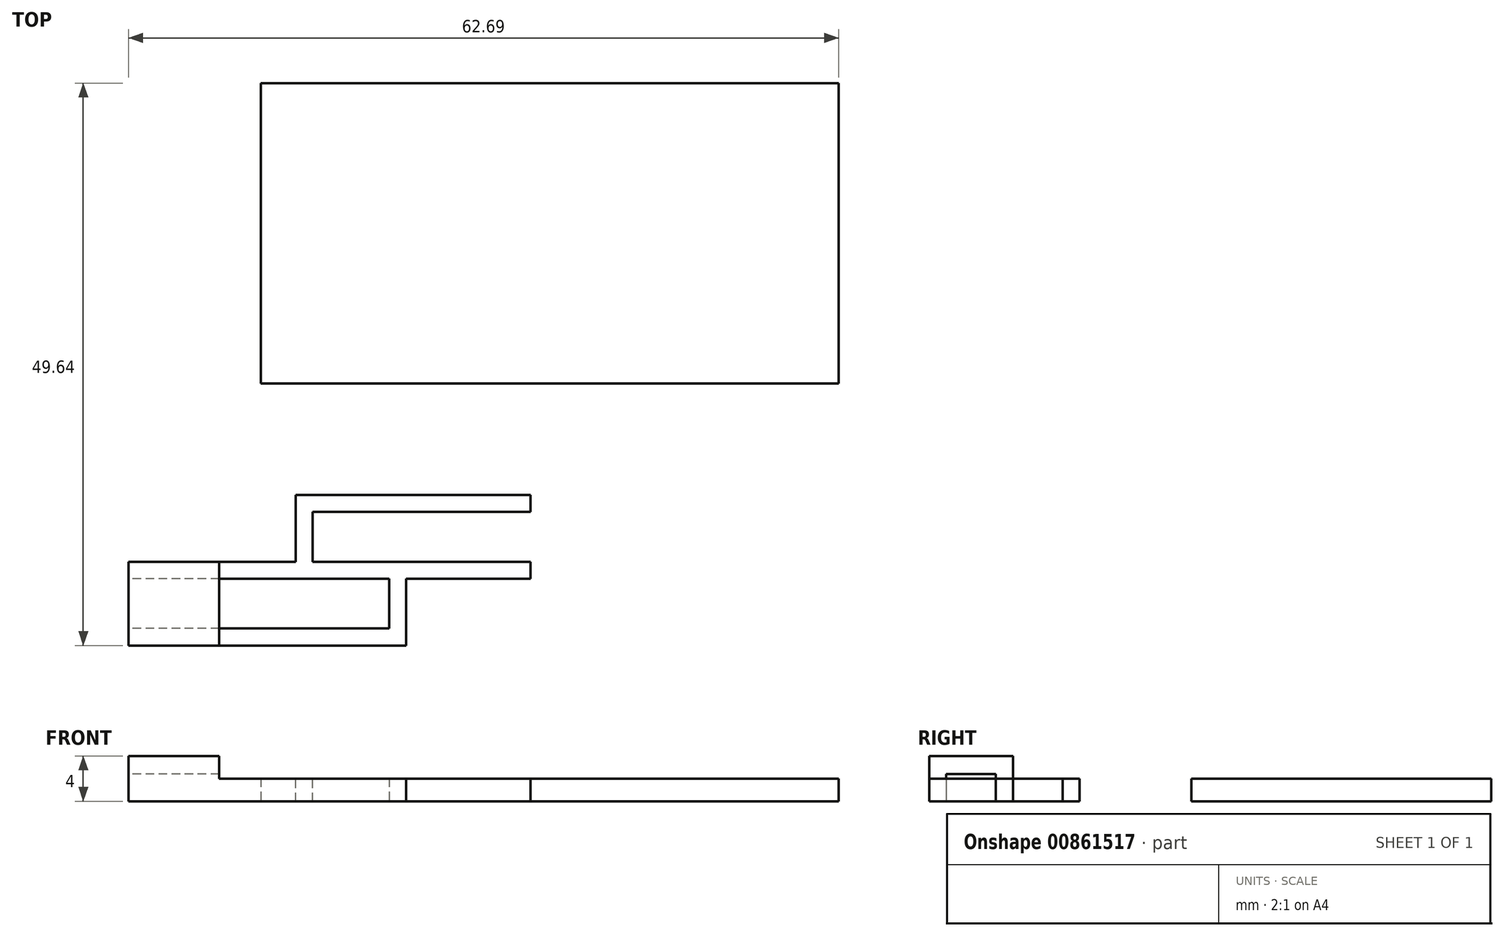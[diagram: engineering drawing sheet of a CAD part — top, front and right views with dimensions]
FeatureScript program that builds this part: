
annotation { "Feature Type Name" : "Feature", "Feature Type Description" : "" }
export const myFeature = defineFeature(function(context is Context, id is Id, definition is map)
    precondition{}
    {
        {
            var Q0;
            Q0=qCreatedBy(makeId("Top.planeOp"),FACE);
            var sketch = newSketch(context, id + "F0", { "sketchPlane" : qUnion([Q0])});
            skLineSegment(sketch, "E0.bottom", {"start": v(25.5, -13.25) * mm, "end": v(-25.5, -13.25) * mm});
            skLineSegment(sketch, "E0.top", {"start": v(25.5, 13.25) * mm, "end": v(-25.5, 13.25) * mm});
            skLineSegment(sketch, "E0.left", {"start": v(25.5, -13.25) * mm, "end": v(25.5, 13.25) * mm});
            skLineSegment(sketch, "E0.right", {"start": v(-25.5, -13.25) * mm, "end": v(-25.5, 13.25) * mm});
            skPoint(sketch, "E0.middle", {"position": v(0, 0) * mm});
            skSolve(sketch);
        }
        {
            var Q0;
            Q0 = qSketchRegion(id + "F0", true);
            extrude(context, id + "F1", {"entities" : qUnion([Q0]), "depth" : 2 * mm, "offsetDistance" : 25.4 * mm});
        }
        {
            var Q0;
            Q0=qCreatedBy(makeId("Top.planeOp"),FACE);
            var sketch = newSketch(context, id + "F2", { "sketchPlane" : qUnion([Q0])});
            skLineSegment(sketch, "E1.bottom", {"start": v(-37.2, -29) * mm, "end": v(-12.7, -29) * mm});
            skLineSegment(sketch, "E1.top", {"start": v(-37.2, -36.4) * mm, "end": v(-12.7, -36.4) * mm});
            skLineSegment(sketch, "E1.left", {"start": v(-37.2, -29) * mm, "end": v(-37.2, -36.4) * mm});
            skLineSegment(sketch, "E1.right", {"start": v(-12.7, -29) * mm, "end": v(-12.7, -36.4) * mm});
            skSolve(sketch);
        }
        {
            var Q0;
            Q0=makeQuery(id+"F2.imprint","IMPRINT",FACE,{"disambiguationData":[TD([[makeQuery(id+"F2.imprint","IMPRINT",EDGE,{"derivedFrom":sQuery(id+"F2.wireOp",EDGE,"E1.bottom")}),-1.0]])]});
            extrude(context, id + "F3", {"entities" : qUnion([Q0]), "depth" : 4 * mm, "offsetDistance" : 25 * mm});
        }
        {
            var Q0;
            Q0=makeQuery(id+"F3.opExtrude","SWEPT_FACE",FACE,{"disambiguationData":[OSD([sQuery(id+"F2.wireOp",EDGE,"E1.left")])]});
            var sketch = newSketch(context, id + "F4", { "sketchPlane" : qUnion([Q0])});
            skLineSegment(sketch, "E2", {"start": v(32.7, 4) * mm, "end": v(32.7, 0) * mm, "construction": true});
            skLineSegment(sketch, "E3.bottom", {"start": v(30.5, 2.4) * mm, "end": v(34.9, 2.4) * mm});
            skLineSegment(sketch, "E3.top", {"start": v(30.5, 0) * mm, "end": v(34.9, 0) * mm});
            skLineSegment(sketch, "E3.left", {"start": v(30.5, 2.4) * mm, "end": v(30.5, 0) * mm});
            skLineSegment(sketch, "E3.right", {"start": v(34.9, 2.4) * mm, "end": v(34.9, 0) * mm});
            skLineSegment(sketch, "E4", {"start": v(32.7, 2.4) * mm, "end": v(32.7, 0) * mm, "construction": true});
            skSolve(sketch);
        }
        {
            var Q0;
            Q0=makeQuery(id+"F4.imprint","IMPRINT",FACE,{"disambiguationData":[TD([[makeQuery(id+"F4.imprint","IMPRINT",EDGE,{"derivedFrom":sQuery(id+"F4.wireOp",EDGE,"E3.bottom")}),-1.0]])]});
            extrude(context, id + "F5", {"entities" : qUnion([Q0]), "operationType" : NewBodyOperationType.REMOVE, "oppositeDirection" : true, "depth" : 23 * mm, "offsetDistance" : 25 * mm});
        }
        {
            var Q0;
            Q0=makeQuery(id+"F3.opExtrude","SWEPT_FACE",FACE,{"disambiguationData":[OSD([sQuery(id+"F2.wireOp",EDGE,"E1.top")])]});
            var sketch = newSketch(context, id + "F6", { "sketchPlane" : qUnion([Q0])});
            skLineSegment(sketch, "E5", {"start": v(-12.7, 2) * mm, "end": v(-29.2, 2) * mm, "construction": true});
            skLineSegment(sketch, "E6", {"start": v(-29.2, 2) * mm, "end": v(-29.2, 0) * mm, "construction": true});
            skLineSegment(sketch, "E7", {"start": v(-29.2, 2) * mm, "end": v(-29.2, 4) * mm});
            skLineSegment(sketch, "E8", {"start": v(-29.2, 2) * mm, "end": v(-12.7, 2) * mm});
            skSolve(sketch);
        }
        {
            var Q0;
            Q0 = qSketchRegion(id + "F6", true);
            var Q1;
            {var subQ0=sQuery(id+"F6.wireOp",EDGE,"E7");Q1=makeQuery(id+"F6.imprint","IMPRINT",FACE,{"disambiguationData":[TD([[makeQuery(id+"F6.imprint","IMPRINT",EDGE,{"derivedFrom":subQ0}),-1.0]])]});}
            extrude(context, id + "F7", {"entities" : qUnion([Q0, Q1]), "operationType" : NewBodyOperationType.REMOVE, "endBound" : BoundingType.THROUGH_ALL, "oppositeDirection" : true, "depth" : 25 * mm, "offsetDistance" : 25 * mm});
        }
        {
            var Q0;
            Q0=makeQuery(id+"F3.opExtrude","SWEPT_BODY",BODY,{"disambiguationData":[OSD([sQuery(id+"F2.wireOp",EDGE,"E1.bottom"),sQuery(id+"F2.wireOp",EDGE,"E1.top"),sQuery(id+"F2.wireOp",EDGE,"E1.left"),sQuery(id+"F2.wireOp",EDGE,"E1.right")])]});
            var Q1;
            Q1=qCreatedBy(makeId("Front.planeOp"),FACE);
            mirror(context, id + "F8", {"entities" : qUnion([Q0]), "mirrorPlane" : qUnion([Q1])});
        }
        {
            var Q0;
            Q0=makeQuery(id+"F3.opExtrude","SWEPT_BODY",BODY,{"disambiguationData":[OSD([sQuery(id+"F2.wireOp",EDGE,"E1.bottom"),sQuery(id+"F2.wireOp",EDGE,"E1.top"),sQuery(id+"F2.wireOp",EDGE,"E1.left"),sQuery(id+"F2.wireOp",EDGE,"E1.right")])]});
            var Q1;
            Q1=qCreatedBy(makeId("Right.planeOp"),FACE);
            mirror(context, id + "F9", {"entities" : qUnion([Q0]), "mirrorPlane" : qUnion([Q1])});
        }
        {
            var Q0;
            Q0=makeQuery(id+"F9.opPattern","COPY",EDGE,{"derivedFrom":makeQuery(id+"F3.opExtrude","CAP_EDGE",EDGE,{"disambiguationData":[OSD([sQuery(id+"F2.wireOp",EDGE,"E1.top")])],"isStart":false}),"instanceName":"1"});
            fillet(context, id + "F10", {"entities" : qUnion([Q0]), "radius" : 1.5 * mm, "tangentPropagation" : true, "allowEdgeOverflow" : false});
        }
        {
            var Q0;
            Q0=makeQuery(id+"F9.opPattern","COPY",EDGE,{"derivedFrom":makeQuery(id+"F3.opExtrude","CAP_EDGE",EDGE,{"disambiguationData":[OSD([sQuery(id+"F2.wireOp",EDGE,"E1.bottom")])],"isStart":false}),"instanceName":"1"});
            fillet(context, id + "F11", {"entities" : qUnion([Q0]), "radius" : 1.5 * mm, "tangentPropagation" : true, "allowEdgeOverflow" : false});
        }
        {
            var Q0;
            Q0=makeQuery(id+"F9.opPattern","COPY",BODY,{"derivedFrom":makeQuery(id+"F3.opExtrude","SWEPT_BODY",BODY,{"disambiguationData":[OSD([sQuery(id+"F2.wireOp",EDGE,"E1.bottom"),sQuery(id+"F2.wireOp",EDGE,"E1.top"),sQuery(id+"F2.wireOp",EDGE,"E1.left"),sQuery(id+"F2.wireOp",EDGE,"E1.right")])]}),"instanceName":"1"});
            deleteBodies(context, id + "F12", {"entities" : qUnion([Q0])});
        }
        {
            var Q0;
            Q0=makeQuery(id+"F8.opPattern","COPY",BODY,{"derivedFrom":makeQuery(id+"F3.opExtrude","SWEPT_BODY",BODY,{"disambiguationData":[OSD([sQuery(id+"F2.wireOp",EDGE,"E1.bottom"),sQuery(id+"F2.wireOp",EDGE,"E1.top"),sQuery(id+"F2.wireOp",EDGE,"E1.left"),sQuery(id+"F2.wireOp",EDGE,"E1.right")])]}),"instanceName":"1"});
            deleteBodies(context, id + "F13", {"entities" : qUnion([Q0])});
        }
        {
            var Q0;
            Q0=makeQuery(id+"F3.opExtrude","SWEPT_FACE",FACE,{"disambiguationData":[OSD([sQuery(id+"F2.wireOp",EDGE,"E1.right")])]});
            var sketch = newSketch(context, id + "F14", { "sketchPlane" : qUnion([Q0])});
            skLineSegment(sketch, "E9", {"start": v(-30.5, 0) * mm, "end": v(-30.5, 2) * mm});
            skSolve(sketch);
        }
        {
            var Q0;
            Q0 = qSketchRegion(id + "F14", true);
            var Q1;
            {var subQ0=sQuery(id+"F14.wireOp",EDGE,"E9");Q1=makeQuery(id+"F14.imprint","IMPRINT",FACE,{"disambiguationData":[TD([[makeQuery(id+"F14.imprint","IMPRINT",EDGE,{"derivedFrom":subQ0}),-1.0]])]});}
            extrude(context, id + "F15", {"entities" : qUnion([Q0, Q1]), "operationType" : NewBodyOperationType.ADD, "depth" : 11 * mm, "offsetDistance" : 25 * mm});
        }
        {
            var Q0;
            {var subQ0=sQuery(id+"F2.wireOp",EDGE,"E1.bottom");Q0=makeQuery(id+"F15.boolean.opBoolean","MERGE",FACE,{"derivedFrom":[makeQuery(id+"F3.opExtrude","SWEPT_FACE",FACE,{"disambiguationData":[OSD([subQ0])]}),makeQuery(id+"F15.opExtrude","SWEPT_FACE",FACE,{"disambiguationData":[OSD([subQ0,sQuery(id+"F2.wireOp",EDGE,"E1.right")])]})]});}
            var sketch = newSketch(context, id + "F16", { "sketchPlane" : qUnion([Q0])});
            skLineSegment(sketch, "E10", {"start": v(29.2, 2) * mm, "end": v(29.2, 0) * mm, "construction": true});
            skLineSegment(sketch, "E11", {"start": v(29.2, 0) * mm, "end": v(14.2, 0) * mm, "construction": true});
            skLineSegment(sketch, "E12", {"start": v(21.7, 0) * mm, "end": v(21.7, 2) * mm, "construction": true});
            skLineSegment(sketch, "E13.bottom", {"start": v(20.94, 0) * mm, "end": v(22.44, 0) * mm});
            skLineSegment(sketch, "E13.top", {"start": v(20.94, 2) * mm, "end": v(22.44, 2) * mm});
            skLineSegment(sketch, "E13.left", {"start": v(20.94, 0) * mm, "end": v(20.94, 2) * mm});
            skLineSegment(sketch, "E13.right", {"start": v(22.44, 0) * mm, "end": v(22.44, 2) * mm});
            skLineSegment(sketch, "E14", {"start": v(21.7, 2) * mm, "end": v(21.7, 0) * mm, "construction": true});
            skSolve(sketch);
        }
        {
            var Q0;
            Q0=makeQuery(id+"F16.imprint","IMPRINT",FACE,{"disambiguationData":[TD([[makeQuery(id+"F16.imprint","IMPRINT",EDGE,{"derivedFrom":sQuery(id+"F16.wireOp",EDGE,"E13.bottom")}),-1.0]])]});
            extrude(context, id + "F17", {"entities" : qUnion([Q0]), "operationType" : NewBodyOperationType.ADD, "depth" : 5.9 * mm, "offsetDistance" : 25 * mm});
        }
        {
            var Q0;
            Q0=makeQuery(id+"F17.opExtrude","SWEPT_FACE",FACE,{"disambiguationData":[OSD([sQuery(id+"F16.wireOp",EDGE,"E13.left")])]});
            var sketch = newSketch(context, id + "F18", { "sketchPlane" : qUnion([Q0])});
            skLineSegment(sketch, "E15", {"start": v(-23.1, 1) * mm, "end": v(-24.6, 1) * mm, "construction": true});
            skLineSegment(sketch, "E16", {"start": v(-24.6, 2) * mm, "end": v(-24.6, 0) * mm});
            skSolve(sketch);
        }
        {
            var Q0;
            {var subQ0=sQuery(id+"F18.wireOp",EDGE,"E16");Q0=makeQuery(id+"F18.imprint","IMPRINT",FACE,{"disambiguationData":[TD([[makeQuery(id+"F18.imprint","IMPRINT",EDGE,{"derivedFrom":subQ0}),1.0]])]});}
            extrude(context, id + "F19", {"entities" : qUnion([Q0]), "operationType" : NewBodyOperationType.ADD, "depth" : 19.25 * mm, "offsetDistance" : 25 * mm});
        }
    });
